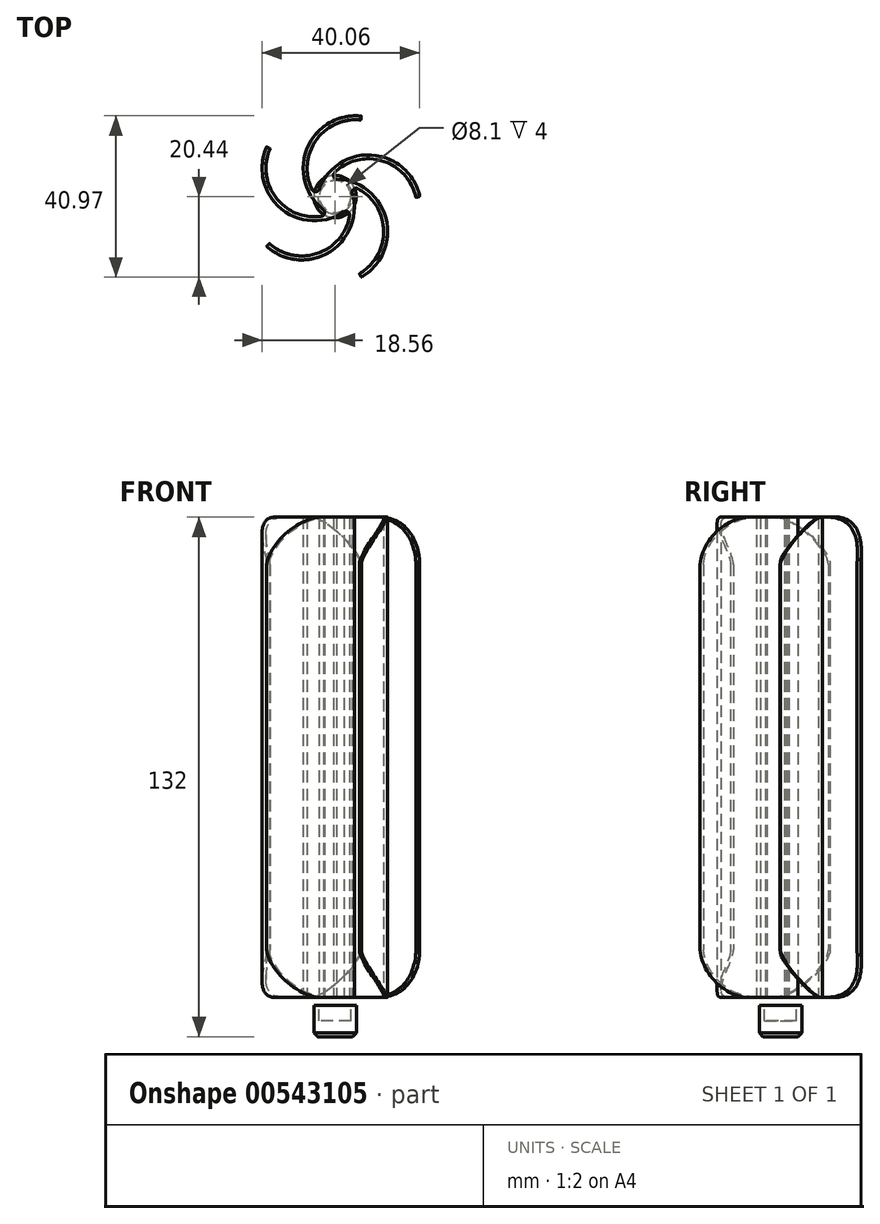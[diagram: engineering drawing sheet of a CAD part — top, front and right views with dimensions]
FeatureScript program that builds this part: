
annotation { "Feature Type Name" : "Feature", "Feature Type Description" : "" }
export const myFeature = defineFeature(function(context is Context, id is Id, definition is map)
    precondition{}
    {
        {
            assignVariable(context, id + "F0", {"name" : "coreLength", "anyValue" : 125});
        }
        {
            var Q0;
            Q0=qCreatedBy(makeId("Top.planeOp"),FACE);
            var sketch = newSketch(context, id + "F1", { "sketchPlane" : qUnion([Q0])});
            skCircle(sketch, "E0", {"center": v(0, 0) * mm, "radius": 4.45 * mm});
            skArc(sketch, "E1", {"start": v(6.67, -20.44) * mm, "mid": v(12.88, -5.44) * mm, "end": v(0, 4.45) * mm});
            skCircle(sketch, "E2", {"center": v(0, 0) * mm, "radius": 21.5 * mm, "construction": true});
            skLineSegment(sketch, "E3", {"start": v(0, 0) * mm, "end": v(0, 4.45) * mm, "construction": true});
            skArc(sketch, "E4", {"start": v(6.17, -19.57) * mm, "mid": v(12.24, -7.32) * mm, "end": v(3.28, 3) * mm});
            skLineSegment(sketch, "E5", {"start": v(6.67, -20.44) * mm, "end": v(6.17, -19.57) * mm});
            skLineSegment(sketch, "E6", {"start": v(6.17, -19.57) * mm, "end": v(0, -8.89) * mm, "construction": true});
            skSolve(sketch);
        }
        {
            var Q0;
            Q0 = qSketchRegion(id + "F1", true);
            extrude(context, id + "F2", {"entities" : qUnion([Q0]), "depth" : (getVariable(context, 'coreLength') - 3) * mm, "offsetDistance" : 25 * mm});
        }
        {
            var Q0;
            Q0=qCreatedBy(makeId("Right.planeOp"),FACE);
            var sketch = newSketch(context, id + "F3", { "sketchPlane" : qUnion([Q0])});
            skLineSegment(sketch, "E7", {"start": v(0, 0) * mm, "end": v(0, 122) * mm, "construction": true});
            skSolve(sketch);
        }
        {
            var Q0;
            Q0=makeQuery(id+"F2.opExtrude","CAP_EDGE",EDGE,{"disambiguationData":[OSD([sQuery(id+"F1.wireOp",EDGE,"E5")])],"isStart":false});
            var Q1;
            Q1=makeQuery(id+"F2.opExtrude","CAP_EDGE",EDGE,{"disambiguationData":[OSD([sQuery(id+"F1.wireOp",EDGE,"E5")])],"isStart":true});
            fillet(context, id + "F4", {"entities" : qUnion([Q0, Q1]), "radius" : 12 * mm, "tangentPropagation" : true, "rho" : .2, "crossSection" : FilletCrossSection.CONIC, "allowEdgeOverflow" : false});
        }
        {
            var Q0;
            Q0=makeQuery(id+"F2.opExtrude","SWEPT_EDGE",EDGE,{"disambiguationData":[OSD([sQuery(id+"F1.wireOp",EDGE,"E0"),sQuery(id+"F1.wireOp",EDGE,"E4")])]});
            fillet(context, id + "F5", {"entities" : qUnion([Q0]), "radius" : 1 * mm, "tangentPropagation" : true, "allowEdgeOverflow" : false});
        }
        {
            var Q0;
            Q0=makeQuery(id+"F2.opExtrude","SWEPT_BODY",BODY,{"disambiguationData":[OSD([sQuery(id+"F1.wireOp",EDGE,"E0"),sQuery(id+"F1.wireOp",EDGE,"E1"),sQuery(id+"F1.wireOp",EDGE,"E4"),sQuery(id+"F1.wireOp",EDGE,"E5")])]});
            var Q1;
            Q1=sQuery(id+"F3.wireOp",EDGE,"E7");
            circularPattern(context, id + "F6", {"operationType" : NewBodyOperationType.ADD, "entities" : qUnion([Q0]), "axis" : qUnion([Q1]), "angle" : 360 * degree, "instanceCount" : 5, "equalSpace" : true});
        }
        {
            assignVariable(context, id + "F7", {"name" : "insetDepth", "anyValue" : 8});
        }
        {
            assignVariable(context, id + "F8", {"name" : "magnetThickness", "anyValue" : 5});
        }
        {
            var Q0;
            Q0=qCreatedBy(makeId("Top.planeOp"),FACE);
            cPlane(context, id + "F9", {"entities" : qUnion([Q0]), "cplaneType" : CPlaneType.OFFSET, "offset" : 2 * mm, "oppositeDirection" : true, "width" : 150 * mm, "height" : 150 * mm});
        }
        {
            var Q0;
            Q0=qCreatedBy(id+"F9.planeOp",FACE);
            var sketch = newSketch(context, id + "F10", { "sketchPlane" : qUnion([Q0])});
            skCircle(sketch, "E8", {"center": v(0, 0) * mm, "radius": 5.4 * mm});
            skCircle(sketch, "E9", {"center": v(0, 0) * mm, "radius": 4.05 * mm});
            skSolve(sketch);
        }
        {
            var Q0;
            Q0 = qSketchRegion(id + "F10", true);
            extrude(context, id + "F11", {"entities" : qUnion([Q0]), "oppositeDirection" : true, "depth" : (getVariable(context, 'magnetThickness') - 1) * mm, "offsetDistance" : 25 * mm});
        }
        {
            var Q0;
            Q0=makeQuery(id+"F11.opExtrude","CAP_FACE",FACE,{"disambiguationData":[OSD([sQuery(id+"F10.wireOp",EDGE,"E8"),sQuery(id+"F10.wireOp",EDGE,"E9")])],"isStart":false});
            var sketch = newSketch(context, id + "F12", { "sketchPlane" : qUnion([Q0])});
            skCircle(sketch, "E10.0", {"center": v(0, 0) * mm, "radius": 5.4 * mm});
            skSolve(sketch);
        }
        {
            var Q0;
            Q0 = qSketchRegion(id + "F12", true);
            extrude(context, id + "F13", {"entities" : qUnion([Q0]), "operationType" : NewBodyOperationType.ADD, "depth" : (getVariable(context, 'insetDepth') - getVariable(context, 'magnetThickness') + 1) * mm, "offsetDistance" : 25 * mm});
        }
        {
            var Q0;
            Q0=makeQuery(id+"F13.opExtrude","CAP_EDGE",EDGE,{"disambiguationData":[OSD([sQuery(id+"F12.wireOp",EDGE,"E10.0")])],"isStart":false});
            chamfer(context, id + "F14", {"entities" : qUnion([Q0]), "width" : 1 * mm, "tangentPropagation" : true});
        }
    });
